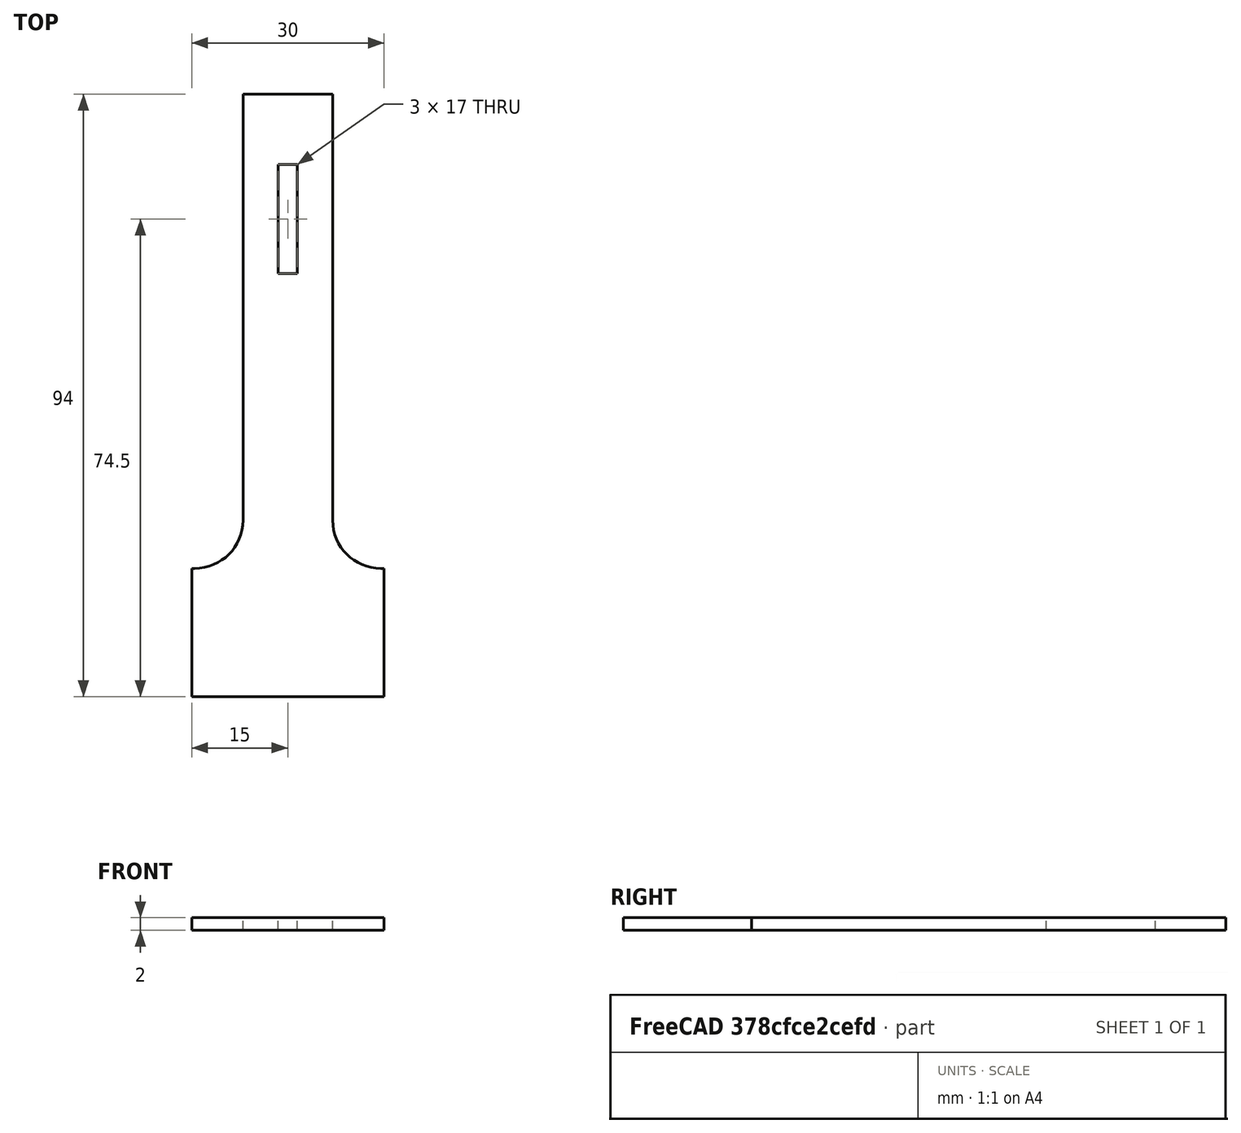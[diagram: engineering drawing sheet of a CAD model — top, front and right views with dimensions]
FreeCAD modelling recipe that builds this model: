
FCSTD DOCUMENT  (FreeCAD 0.18R16146 (Git))
Label: Support_boucle
License: All rights reserved
LicenseURL: http://en.wikipedia.org/wiki/All_rights_reserved
objects: Sketcher::SketchObject×2, PartDesign::Pad×1, PartDesign::Body×1, Drawing::FeatureViewPart×1, Drawing::FeaturePage×1
note: 5 computed .brp shape members not serialized (recipe doc carries the construction recipe); baked Part::Feature solids carry a one-line shape summary decoded from their .brp

FEATURE [Sketcher::SketchObject] Sketch
  sketch-geometry (14):
    g0: LineSegment StartX=0 StartY=0 StartZ=0 EndX=30 EndY=0 EndZ=0
    g1: LineSegment StartX=30 StartY=0 StartZ=0 EndX=30 EndY=20 EndZ=0
    g2: LineSegment StartX=30 StartY=20 StartZ=0 EndX=29.5 EndY=20 EndZ=0
    g3: LineSegment StartX=0 StartY=20 StartZ=0 EndX=0 EndY=0 EndZ=0
    g4: LineSegment StartX=22 StartY=27.5 StartZ=0 EndX=22 EndY=94 EndZ=0
    g5: LineSegment StartX=22 StartY=94 StartZ=0 EndX=8 EndY=94 EndZ=0
    g6: LineSegment StartX=8 StartY=94 StartZ=0 EndX=8 EndY=27.5 EndZ=0
    g7: ArcOfCircle CenterX=29.5 CenterY=27.5 CenterZ=0 NormalX=0 NormalY=0 NormalZ=1 AngleXU=0 Radius=7.5 StartAngle=3.14159 EndAngle=4.71239
    g8: LineSegment StartX=0 StartY=20 StartZ=0 EndX=0.5 EndY=20 EndZ=0
    g9: ArcOfCircle CenterX=0.5 CenterY=27.5 CenterZ=0 NormalX=0 NormalY=0 NormalZ=1 AngleXU=0 Radius=7.5 StartAngle=4.71239 EndAngle=6.28319
    g10: LineSegment StartX=13.5 StartY=83 StartZ=0 EndX=16.5 EndY=83 EndZ=0
    g11: LineSegment StartX=16.5 StartY=83 StartZ=0 EndX=16.5 EndY=66 EndZ=0
    g12: LineSegment StartX=16.5 StartY=66 StartZ=0 EndX=13.5 EndY=66 EndZ=0
    g13: LineSegment StartX=13.5 StartY=66 StartZ=0 EndX=13.5 EndY=83 EndZ=0
  constraints (39):
    c: Coincident(g0,g1)
    c: Coincident(g1,g2)
    c: Coincident(g3,g0)
    c: Horizontal(g0)
    c: Horizontal(g2)
    c: Vertical(g1)
    c: Vertical(g3)
    c: Coincident(g0,g-1)
    c: DistanceY(g1,g1) = 20
    c: DistanceX(g0,g0) = 30
    c: Coincident(g4,g5)
    c: Coincident(g5,g6)
    c: Horizontal(g5)
    c: Vertical(g4)
    c: Vertical(g6)
    c: Distance(g3,g6) = 8
    c: DistanceX(g5,g5) = 14
    c: Tangent(g2,g7) = 1.5708
    c: Tangent(g4,g7) = 1.5708
    c: Coincident(g8,g3)
    c: Horizontal(g8)
    c: Tangent(g8,g9) = -1.5708
    c: Tangent(g6,g9) = 1.5708
    c: Radius(g7) = 7.5
    c: DistanceY(g3,g3) = 20
    c: Radius(g9) = 7.5
    c: Coincident(g10,g11)
    c: Coincident(g11,g12)
    c: Coincident(g12,g13)
    c: Coincident(g13,g10)
    c: Horizontal(g10)
    c: Horizontal(g12)
    c: Vertical(g11)
    c: Vertical(g13)
    c: DistanceX(g12,g12) = 3
    c: DistanceY(g11,g11) = 17
    c: Distance(g10,g5) = 11
    c: Distance(g10,g6) = 5.5
    c: Distance(g1,g5) = 74
FEATURE [Sketcher::SketchObject] CopySketch
  sketch-geometry (14):
    g0: LineSegment StartX=0 StartY=0 StartZ=0 EndX=30 EndY=0 EndZ=0
    g1: LineSegment StartX=30 StartY=0 StartZ=0 EndX=30 EndY=20 EndZ=0
    g2: LineSegment StartX=30 StartY=20 StartZ=0 EndX=29.5 EndY=20 EndZ=0
    g3: LineSegment StartX=0 StartY=20 StartZ=0 EndX=0 EndY=0 EndZ=0
    g4: LineSegment StartX=22 StartY=27.5 StartZ=0 EndX=22 EndY=94 EndZ=0
    g5: LineSegment StartX=22 StartY=94 StartZ=0 EndX=8 EndY=94 EndZ=0
    g6: LineSegment StartX=8 StartY=94 StartZ=0 EndX=8 EndY=27.5 EndZ=0
    g7: ArcOfCircle CenterX=29.5 CenterY=27.5 CenterZ=0 NormalX=0 NormalY=0 NormalZ=1 AngleXU=0 Radius=7.5 StartAngle=3.14159 EndAngle=4.71239
    g8: LineSegment StartX=0 StartY=20 StartZ=0 EndX=0.5 EndY=20 EndZ=0
    g9: ArcOfCircle CenterX=0.5 CenterY=27.5 CenterZ=0 NormalX=0 NormalY=0 NormalZ=1 AngleXU=0 Radius=7.5 StartAngle=4.71239 EndAngle=6.28319
    g10: LineSegment StartX=13.5 StartY=83 StartZ=0 EndX=16.5 EndY=83 EndZ=0
    g11: LineSegment StartX=16.5 StartY=83 StartZ=0 EndX=16.5 EndY=66 EndZ=0
    g12: LineSegment StartX=16.5 StartY=66 StartZ=0 EndX=13.5 EndY=66 EndZ=0
    g13: LineSegment StartX=13.5 StartY=66 StartZ=0 EndX=13.5 EndY=83 EndZ=0
  constraints (39):
    c: Coincident(g0,g1)
    c: Coincident(g1,g2)
    c: Coincident(g3,g0)
    c: Horizontal(g0)
    c: Horizontal(g2)
    c: Vertical(g1)
    c: Vertical(g3)
    c: Coincident(g0,g-1)
    c: DistanceY(g1,g1) = 20
    c: DistanceX(g0,g0) = 30
    c: Coincident(g4,g5)
    c: Coincident(g5,g6)
    c: Horizontal(g5)
    c: Vertical(g4)
    c: Vertical(g6)
    c: Distance(g3,g6) = 8
    c: DistanceX(g5,g5) = 14
    c: Tangent(g2,g7) = 1.5708
    c: Tangent(g4,g7) = 1.5708
    c: Coincident(g8,g3)
    c: Horizontal(g8)
    c: Tangent(g8,g9) = -1.5708
    c: Tangent(g6,g9) = 1.5708
    c: Radius(g7) = 7.5
    c: DistanceY(g3,g3) = 20
    c: Radius(g9) = 7.5
    c: Coincident(g10,g11)
    c: Coincident(g11,g12)
    c: Coincident(g12,g13)
    c: Coincident(g13,g10)
    c: Horizontal(g10)
    c: Horizontal(g12)
    c: Vertical(g11)
    c: Vertical(g13)
    c: DistanceX(g12,g12) = 3
    c: DistanceY(g11,g11) = 17
    c: Distance(g10,g5) = 11
    c: Distance(g10,g6) = 5.5
    c: Distance(g1,g5) = 74
FEATURE [PartDesign::Pad] Pad
  Length = 2
  Length2 = 100
  Profile = -> CopySketch
  Type = 0
FEATURE [PartDesign::Body] Body
  Group = -> [Pad]
  Origin = -> Origin
  Tip = -> Pad
FEATURE [Drawing::FeatureViewPart] Ortho  label="Ortho_0_0"
  Direction = (0,0,1)
  HiddenWidth = 0.15
  LineWidth = 0.35
  Rotation = 90
  ShowHiddenLines = false
  ShowSmoothLines = false
  Source = -> Pad
  Tolerance = 0.05
  ViewResult = <g id="Ortho_0_0"\n   transform="rotate(90,101.5,71) translate(101.5,71) scale(1,1)"\n  >\n<g   fill="none"\n   stroke="rgb(0, 0, 0)"\n   stroke-linecap="butt"\n   stroke-linejoin="miter"\n   stroke-width="0.350000"\n   transform="scale(1,-1)"\n  >\n<path id= "1" d=" M 0 20 L 0 0 " />\n<path id= "2" d=" M 0 0 L 30 0 " />\n<path id= "3" d=" M 30 0 L 30 20 " />\n<path id= "4" d=" M 30 20 L 29.5 20 " />\n<path d="M22 27.5 A7.5 7.5 0 0 1 29.5 20" /><path id= "6" d=" M 22 27.5 L 22 94 " />\n<path id= "7" d=" M 22 94 L 8 94 " />\n<path id= "8" d=" M 8 94 L 8 27.5 " />\n<path d="M0.5 20 A7.5 7.5 0 0 1 8 27.5" /><path id= "10" d=" M 0 20 L 0.5 20 " />\n<path id= "11" d=" M 13.5 83 L 16.5 83 " />\n<path id= "12" d=" M 16.5 83 L 16.5 66 " />\n<path id= "13" d=" M 16.5 66 L 13.5 66 " />\n<path id= "14" d=" M 13.5 66 L 13.5 83 " />\n</g>\n</g>
  Visible = false
  X = 101.5
  Y = 71
FEATURE [Drawing::FeaturePage] Page001
  EditableTexts = Jérôme Dubois | Support de boucle | FreeCAD DRAWING | A4 | 1/1 | 1 | 01 | 01 | 28/12/2021 | REV A
  Group = -> [Ortho]
  Template = <path>
note: 1 file-system path scrubbed to <path> (originals preserved in the JSON sidecar)
